# Revit family: J2 PET Felt Conic Cloud Grid
name_source: partatom
category: Specialty Equipment
units: mm (PartAtom-declared; Revit-internal decimal feet)

## family parameters
Always vertical = Yes
Cut with Voids When Loaded = No
Part Type = Normal
Room Calculation Point = No
Round Connector Dimension = Use Diameter
Shared = No
Work Plane-Based = No

## types (3) — shared parameters
Default Elevation = 0' - 0"
Felt Color = <By Category>
Manufacturer = J2 Systems
Model = Conic Cloud Grid
Product Line = Ceiling System
Release Date = 2019
Style Number = CSCGCO
URL = https://www.j2systems.net

## per-type parameters (varying)
| type | Baffle Height B | Baffle Height C | Baffle Height at Edges | Default Baffle Spacing "X" | Default Baffle Spacing "Y" | Default End Spacing "X" | Default End Spacing "Y" | Nominal Length "X" (Max. 8') | Nominal Width "Y" (Max. 8') | Overall Baffle Height |
| Conic Cloud Grid 8'x8' | 0' - 9 11/32" | 0' - 7 21/32" | 0' - 6" | 1' - 1 23/32" | 1' - 1 23/32" | 0' - 6 27/32" | 0' - 6 27/32" | 8' - 0" | 8' - 0" | 0' - 11" |
| Conic Cloud Grid 4'x4' | 0' - 6" | 0' - 5" | 0' - 4" | 0' - 6 27/32" | 0' - 6 27/32" | 0' - 3 7/16" | 0' - 3 7/16" | 4' - 0" | 4' - 0" | 0' - 7" |
| Conic Cloud Grid 6'x6' | 0' - 7 21/32" | 0' - 6 11/32" | 0' - 5" | 0' - 10 9/32" | 0' - 10 9/32" | 0' - 5 5/32" | 0' - 5 5/32" | 6' - 0" | 6' - 0" | 0' - 9" |

## geometry (parser evidence)
native form markers: Blend x8, Sweep x19
no freeform markers — native parametric forms only
